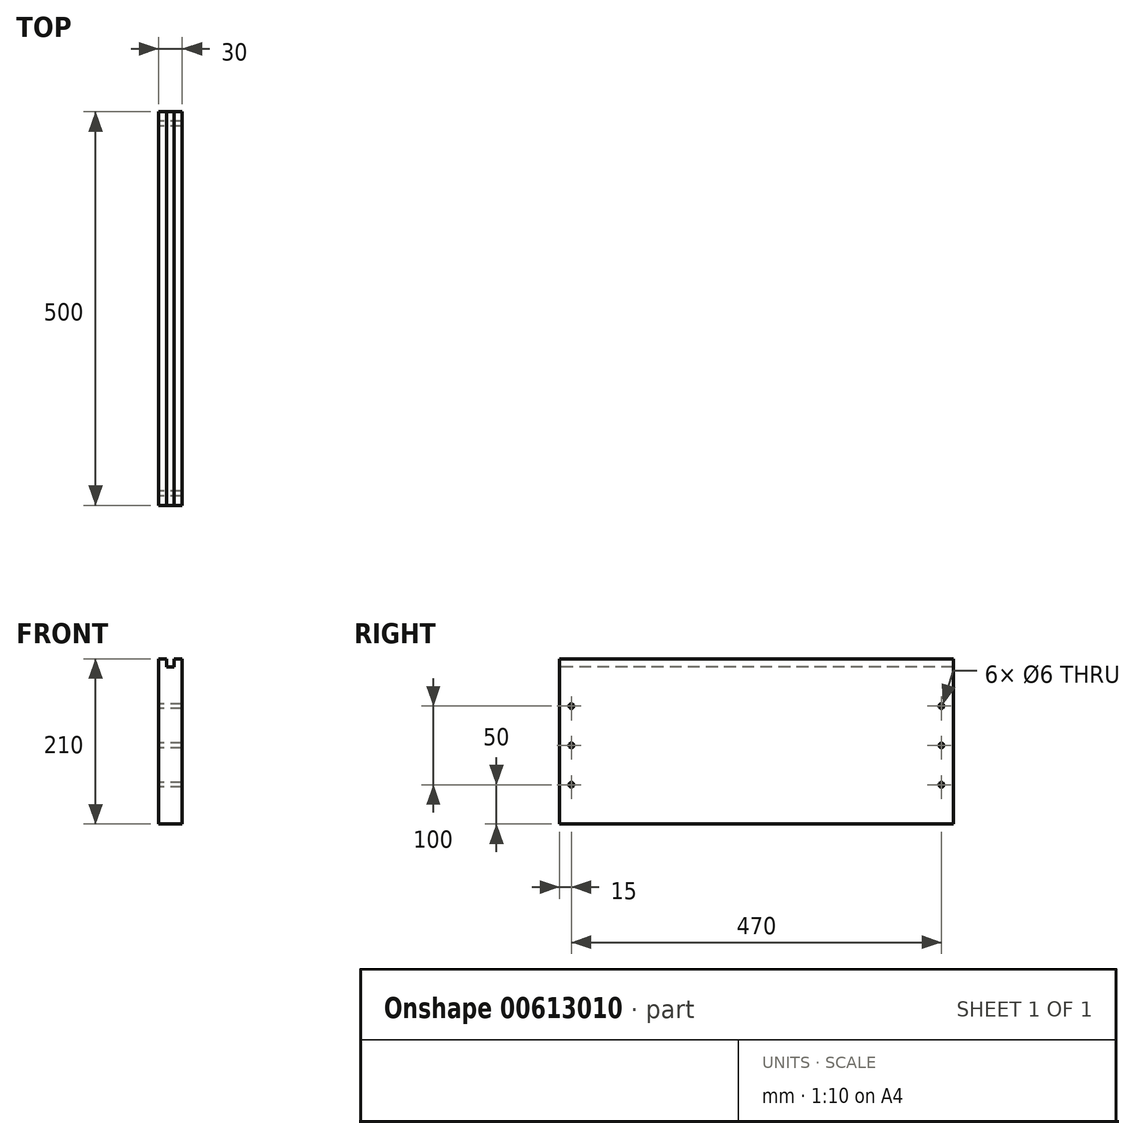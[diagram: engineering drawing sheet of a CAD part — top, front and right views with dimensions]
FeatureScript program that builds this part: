
annotation { "Feature Type Name" : "Feature", "Feature Type Description" : "" }
export const myFeature = defineFeature(function(context is Context, id is Id, definition is map)
    precondition{}
    {
        {
            var Q0;
            Q0=qCreatedBy(makeId("Right.planeOp"),FACE);
            var sketch = newSketch(context, id + "F0", { "sketchPlane" : qUnion([Q0])});
            skLineSegment(sketch, "E0.bottom", {"start": v(250, -100) * mm, "end": v(-250, -100) * mm});
            skLineSegment(sketch, "E0.top", {"start": v(250, 100) * mm, "end": v(-250, 100) * mm});
            skLineSegment(sketch, "E0.left", {"start": v(250, -100) * mm, "end": v(250, 100) * mm});
            skLineSegment(sketch, "E0.right", {"start": v(-250, -100) * mm, "end": v(-250, 100) * mm});
            skPoint(sketch, "E0.middle", {"position": v(0, 0) * mm});
            skCircle(sketch, "E1", {"center": v(-235, 50) * mm, "radius": 3 * mm});
            skCircle(sketch, "E2", {"center": v(235, -50) * mm, "radius": 3 * mm});
            skCircle(sketch, "E3", {"center": v(235, 50) * mm, "radius": 3 * mm});
            skCircle(sketch, "E4", {"center": v(-235, -50) * mm, "radius": 3 * mm});
            skCircle(sketch, "E5", {"center": v(-235, 0) * mm, "radius": 3 * mm});
            skCircle(sketch, "E6", {"center": v(235, 0) * mm, "radius": 3 * mm});
            skSolve(sketch);
        }
        {
            var Q0;
            Q0=qSketchRegion(id+"F0",true);
            extrude(context, id + "F1", {"entities" : qUnion([Q0]), "depth" : 30 * mm, "offsetDistance" : 25 * mm});
        }
        {
            var Q0;
            Q0=makeQuery(id+"F1.opExtrude","SWEPT_FACE",FACE,{"disambiguationData":[OSD([sQuery(id+"F0.wireOp",EDGE,"E0.right")])]});
            var sketch = newSketch(context, id + "F2", { "sketchPlane" : qUnion([Q0])});
            skLineSegment(sketch, "E7.bottom", {"start": v(10, 100) * mm, "end": v(0, 100) * mm});
            skLineSegment(sketch, "E7.top", {"start": v(10, 110) * mm, "end": v(0, 110) * mm});
            skLineSegment(sketch, "E7.left", {"start": v(10, 100) * mm, "end": v(10, 110) * mm});
            skLineSegment(sketch, "E7.right", {"start": v(0, 100) * mm, "end": v(0, 110) * mm});
            skPoint(sketch, "E7.middle", {"position": v(5, 105) * mm});
            skSolve(sketch);
        }
        {
            var Q0;
            Q0=qSketchRegion(id+"F2",true);
            extrude(context, id + "F3", {"entities" : qUnion([Q0]), "operationType" : NewBodyOperationType.ADD, "depth" : -500 * mm, "offsetDistance" : 25 * mm});
        }
        {
            var Q0;
            Q0=makeQuery(id+"F3.boolean.opBoolean","MERGE",FACE,{"derivedFrom":[makeQuery(id+"F1.opExtrude","SWEPT_FACE",FACE,{"disambiguationData":[OSD([sQuery(id+"F0.wireOp",EDGE,"E0.right")])]}),makeQuery(id+"F3.opExtrude","CAP_FACE",FACE,{"disambiguationData":[OSD([sQuery(id+"F2.wireOp",EDGE,"E7.bottom"),sQuery(id+"F2.wireOp",EDGE,"E7.top"),sQuery(id+"F2.wireOp",EDGE,"E7.left"),sQuery(id+"F2.wireOp",EDGE,"E7.right")])],"isStart":true})]});
            var sketch = newSketch(context, id + "F4", { "sketchPlane" : qUnion([Q0])});
            skLineSegment(sketch, "E8.bottom", {"start": v(30, 100) * mm, "end": v(20, 100) * mm});
            skLineSegment(sketch, "E8.top", {"start": v(30, 110) * mm, "end": v(20, 110) * mm});
            skLineSegment(sketch, "E8.left", {"start": v(30, 100) * mm, "end": v(30, 110) * mm});
            skLineSegment(sketch, "E8.right", {"start": v(20, 100) * mm, "end": v(20, 110) * mm});
            skPoint(sketch, "E8.middle", {"position": v(25, 105) * mm});
            skSolve(sketch);
        }
        {
            var Q0;
            Q0=qSketchRegion(id+"F4",true);
            extrude(context, id + "F5", {"entities" : qUnion([Q0]), "operationType" : NewBodyOperationType.ADD, "depth" : -500 * mm, "offsetDistance" : 25 * mm});
        }
    });
